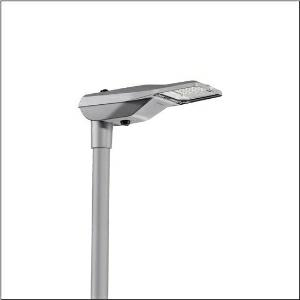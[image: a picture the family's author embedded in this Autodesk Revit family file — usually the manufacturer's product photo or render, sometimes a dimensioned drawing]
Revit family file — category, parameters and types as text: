
# Revit family: streetlight_sl_21_iq_micro___st1_0ab_5xe1m31y08db_79d8
name_source: partatom
category: Lighting Fixtures
units: mm (PartAtom-declared; Revit-internal decimal feet)

## family parameters
Cut with Voids When Loaded = No
Host = Face
Light Source = No
Part Type = Normal
Room Calculation Point = No
Round Connector Dimension = Use Diameter
Shared = No

## types (1)
- --- (1 x LED, 4490 lm, 39.1 W, 3000K)
    Apparent Load = 39 VA
    CIE Flux Codes = 38 73 97 100 100
    Color Rendering = 70
    Color Temperature = 3000K
    Default Elevation = 1800 mm
    Description = Streetlight SL 21 iQ micro, mast luminaire, primary light control with lens, of PMMA, primary optical cover: cover, of toughened safety glass, transparent, light distribution: ST1.0aB, light emission: direct distribution, primary light characteristic: asymmetric, installation type: post-top, side-entry, LED, High Power LED, rated luminous flux: 4.490lm, luminous efficacy: 115lm/W, light colour: 730, colour temperature: 3000K, control gear: iQ-Street Remote, D4i with power reduction, control: pre-setting: logarithmic dimming characteristic, Street-Remote, Auto-Match, Temp-Guard, Lumen-Switch, Night-Set, Smart-Wire, Light-Fading, Desk-Remote (wireless, voltage-free reading and setting of iQ features in the workshop via application-optimized NFC function/RFID function), optimised constant luminous flux control (CLO 2.0), mains connection: 220..240V, AC, 50/60Hz, start of lifetime: 39W, end of service life: 41W, reduction: 17W, luminaire housing, of diecast aluminium, powder-coated, Siteco® metallic grey (DB 702S), corrosivity category C5 mid according to DIN EN ISO 12944, please order mast flange separately, inclination adjustable: 0°, 5°, 10°, 15°, sealing non-destructively replaceable, multi-level sealing system, length: 528mm, width: 235mm, height: 110mm, mast flange for spigot size: 42mm (side-entry): 5XC10008XM4, 60/48mm (side-entry/post-top): 5XC10108XM2, 76/60mm (side-entry/post-top): 5XC10108XM1, mounting height: 4..8m, Smart Interface below and above, protection rating (complete): IP66, insulation class (complete): insulation class II (safety insulation), certification: CE, ENEC, ENEC+, VDE, impact resistance: IK10, permissible operating ambient temperature for outdoor applications: -40..+50°C, standard-compliant lighting for roads and squares, packaging unit: 1 piece

Light Distribution: ST1.0aB
    Height = 110 mm
    Lamp = 1 x LED
    Lamp Light Flux = 4490 lm
    Lamp Power = 39.1 W
    Lamp count = 1
    Length = 528 mm
    Luminous efficacy = 115 lm/W
    Manufacturer = Siteco
    ModVariant = No
    Model = 5XE1M31Y08DB
    Number of Poles = 1
    OnlyDefault = Yes
    Power Factor = 1
    Product Name = Streetlight SL 21 iQ micro | ST1.0aB
    Product group = mast luminaire | pylon top
    ProductGroupID = 6100
    Protection Class = Protection class II
    Protection Degree = IP 66
    RLX_Detail_Level = 1
    RLX_Emergency_Light_Flux = 0 lm
    RLX_Emergency_Type = 0
    RLX_Emergency_Type_DB = No
    RlxData = <blob elided: 98389 chars, md5=818f32ff>
    Socket = socket
    Standby Power = 0 W
    System Light Flux = 4490 lm
    System Power = 39 W
    Type Comments = factory setting: luminous flux: 100 % | dim-lin: 254 | 765 mA
    Type Image = l_1007239.jpg
    URL = http://relux.com
    VarID = @adj_134111
    Voltage = 0 V
    Weight = 0.00 kg
    Width = 235 mm

## geometry (parser evidence)
native form markers: Blend x4, Sweep x12
no freeform markers — native parametric forms only
